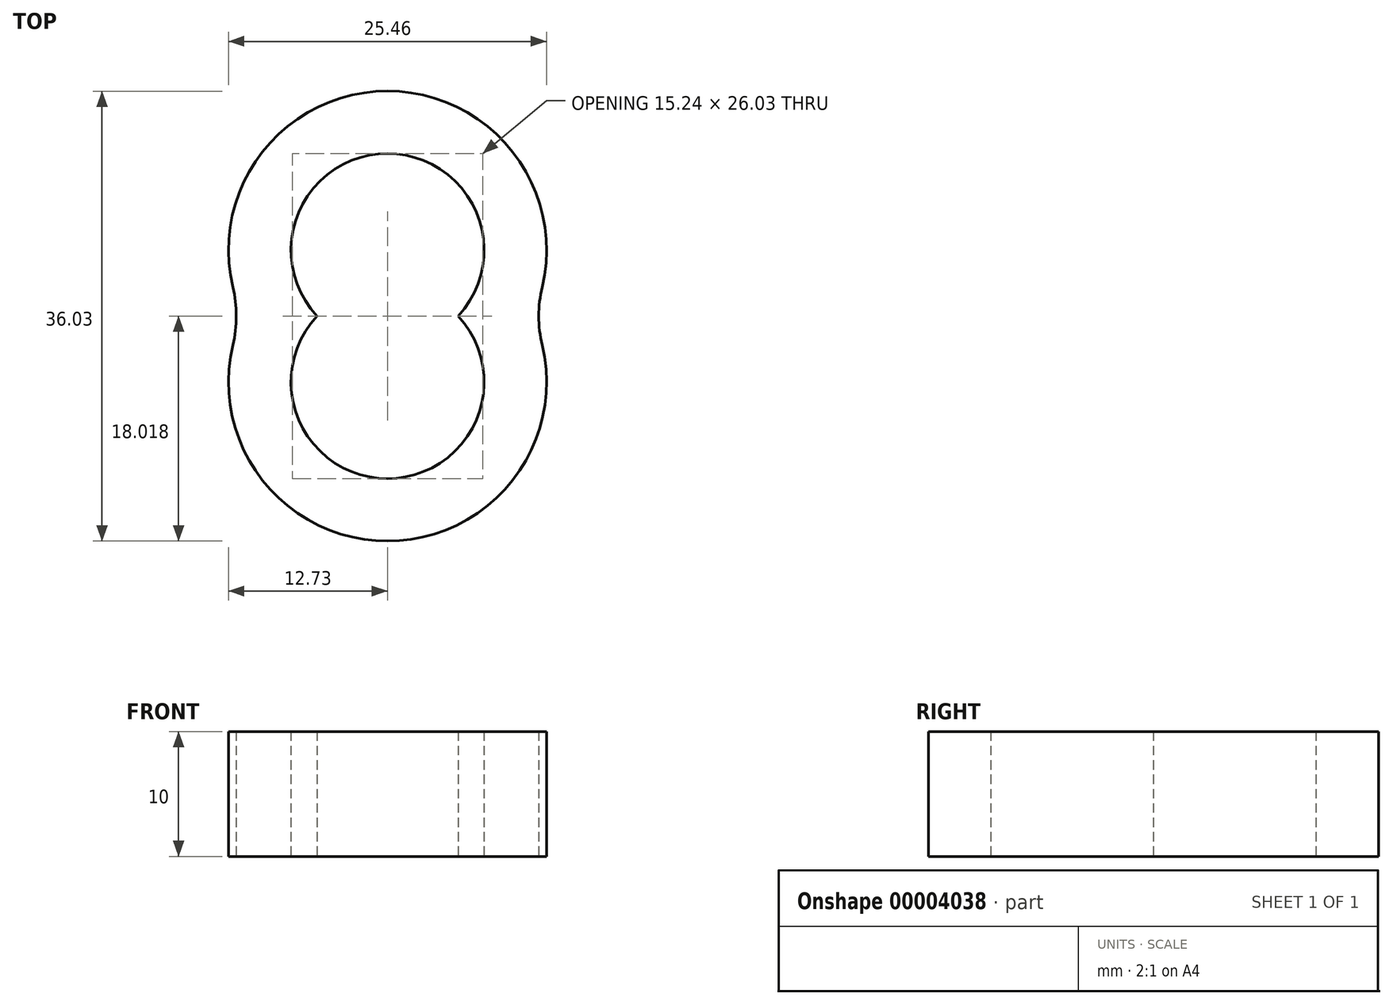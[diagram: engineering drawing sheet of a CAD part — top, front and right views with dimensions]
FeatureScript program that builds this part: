
annotation { "Feature Type Name" : "Feature", "Feature Type Description" : "" }
export const myFeature = defineFeature(function(context is Context, id is Id, definition is map)
    precondition{}
    {
        {
            var Q0;
            Q0=qCreatedBy(makeId("Top.planeOp"),FACE);
            var sketch = newSketch(context, id + "F0", { "sketchPlane" : qUnion([Q0])});
            skArc(sketch, "E0", {"start": v(-78.68, 36.93) * mm, "mid": v(-73.03, 23.91) * mm, "end": v(-67.38, 36.93) * mm});
            skLineSegment(sketch, "E1", {"start": v(-78.68, 36.93) * mm, "end": v(41.42, 36.93) * mm, "construction": true});
            skArc(sketch, "E2.0", {"start": v(-85.41, 34.6) * mm, "mid": v(-73.03, 18.91) * mm, "end": v(-60.65, 34.6) * mm});
            skLineSegment(sketch, "E3", {"start": v(-84.61, 36.93) * mm, "end": v(-78.68, 36.93) * mm});
            skLineSegment(sketch, "E4", {"start": v(-67.38, 36.93) * mm, "end": v(-61.45, 36.93) * mm});
            skArc(sketch, "E5.0.MirrorCS", {"start": v(-78.68, 36.93) * mm, "mid": v(-73.03, 49.94) * mm, "end": v(-67.38, 36.93) * mm});
            skArc(sketch, "E6.0.MirrorCS", {"start": v(-85.41, 39.25) * mm, "mid": v(-73.03, 54.94) * mm, "end": v(-60.65, 39.25) * mm});
            skPoint(sketch, "E7.visualSharp", {"position": v(-61.45, 36.93) * mm});
            skArc(sketch, "E7.filletArc", {"start": v(-60.65, 39.25) * mm, "mid": v(-60.92, 36.93) * mm, "end": v(-60.65, 34.6) * mm});
            skPoint(sketch, "E8.visualSharp", {"position": v(-84.61, 36.93) * mm});
            skArc(sketch, "E8.filletArc", {"start": v(-85.41, 34.6) * mm, "mid": v(-85.14, 36.93) * mm, "end": v(-85.41, 39.25) * mm});
            skArc(sketch, "E9.1.0", {"start": v(-99.44, 9.54) * mm, "mid": v(-103.48, 23.13) * mm, "end": v(-90.79, 16.8) * mm});
            skArc(sketch, "E9.1.1", {"start": v(-106.1, 6.98) * mm, "mid": v(-106.7, 26.96) * mm, "end": v(-87.12, 22.9) * mm});
            skArc(sketch, "E9.1.2", {"start": v(-99.44, 9.54) * mm, "mid": v(-86.75, 3.2) * mm, "end": v(-90.79, 16.8) * mm});
            skArc(sketch, "E9.1.3", {"start": v(-103.1, 3.42) * mm, "mid": v(-83.53, -0.64) * mm, "end": v(-84.13, 19.34) * mm});
            skArc(sketch, "E9.1.4", {"start": v(-87.12, 22.9) * mm, "mid": v(-85.84, 20.95) * mm, "end": v(-84.13, 19.34) * mm});
            skArc(sketch, "E9.1.5", {"start": v(-103.1, 3.42) * mm, "mid": v(-104.39, 5.38) * mm, "end": v(-106.1, 6.98) * mm});
            skArc(sketch, "E9.2.0", {"start": v(-97.73, -24.8) * mm, "mid": v(-109.57, -16.97) * mm, "end": v(-95.77, -13.67) * mm});
            skArc(sketch, "E9.2.1", {"start": v(-101.2, -31.03) * mm, "mid": v(-114.5, -16.1) * mm, "end": v(-96.9, -6.64) * mm});
            skArc(sketch, "E9.2.2", {"start": v(-97.73, -24.8) * mm, "mid": v(-83.94, -21.5) * mm, "end": v(-95.77, -13.67) * mm});
            skArc(sketch, "E9.2.3", {"start": v(-96.61, -31.83) * mm, "mid": v(-79.01, -22.36) * mm, "end": v(-92.31, -7.44) * mm});
            skArc(sketch, "E9.2.4", {"start": v(-96.9, -6.64) * mm, "mid": v(-94.65, -7.3) * mm, "end": v(-92.31, -7.44) * mm});
            skArc(sketch, "E9.2.5", {"start": v(-96.61, -31.83) * mm, "mid": v(-98.86, -31.16) * mm, "end": v(-101.2, -31.03) * mm});
            skArc(sketch, "E9.3.0", {"start": v(-74.36, -50) * mm, "mid": v(-88.46, -51.62) * mm, "end": v(-80, -40.22) * mm});
            skArc(sketch, "E9.3.1", {"start": v(-73, -57) * mm, "mid": v(-92.79, -54.12) * mm, "end": v(-85.39, -35.55) * mm});
            skArc(sketch, "E9.3.2", {"start": v(-74.36, -50) * mm, "mid": v(-65.91, -38.6) * mm, "end": v(-80, -40.22) * mm});
            skArc(sketch, "E9.3.3", {"start": v(-68.98, -54.67) * mm, "mid": v(-61.58, -36.1) * mm, "end": v(-81.36, -33.22) * mm});
            skArc(sketch, "E9.3.4", {"start": v(-85.39, -35.55) * mm, "mid": v(-83.24, -34.62) * mm, "end": v(-81.36, -33.22) * mm});
            skArc(sketch, "E9.3.5", {"start": v(-68.98, -54.67) * mm, "mid": v(-71.13, -55.6) * mm, "end": v(-73, -57) * mm});
            skArc(sketch, "E9.4.0", {"start": v(-40.26, -54.28) * mm, "mid": v(-50.01, -64.58) * mm, "end": v(-50.87, -50.42) * mm});
            skArc(sketch, "E9.4.1", {"start": v(-34.72, -58.77) * mm, "mid": v(-51.72, -69.28) * mm, "end": v(-58, -50.3) * mm});
            skArc(sketch, "E9.4.2", {"start": v(-40.26, -54.28) * mm, "mid": v(-41.11, -40.12) * mm, "end": v(-50.87, -50.42) * mm});
            skArc(sketch, "E9.4.3", {"start": v(-33.13, -54.4) * mm, "mid": v(-39.4, -35.42) * mm, "end": v(-56.4, -45.93) * mm});
            skArc(sketch, "E9.4.4", {"start": v(-58, -50.3) * mm, "mid": v(-56.94, -48.2) * mm, "end": v(-56.4, -45.93) * mm});
            skArc(sketch, "E9.4.5", {"start": v(-33.13, -54.4) * mm, "mid": v(-34.18, -56.5) * mm, "end": v(-34.72, -58.77) * mm});
            skArc(sketch, "E9.5.0", {"start": v(-11.38, -35.64) * mm, "mid": v(-12.23, -49.8) * mm, "end": v(-21.99, -39.5) * mm});
            skArc(sketch, "E9.5.1", {"start": v(-4.25, -35.52) * mm, "mid": v(-10.52, -54.5) * mm, "end": v(-27.53, -44) * mm});
            skArc(sketch, "E9.5.2", {"start": v(-11.38, -35.64) * mm, "mid": v(-21.14, -25.34) * mm, "end": v(-21.99, -39.5) * mm});
            skArc(sketch, "E9.5.3", {"start": v(-5.84, -31.15) * mm, "mid": v(-22.85, -20.64) * mm, "end": v(-29.12, -39.62) * mm});
            skArc(sketch, "E9.5.4", {"start": v(-27.53, -44) * mm, "mid": v(-28.06, -41.71) * mm, "end": v(-29.12, -39.62) * mm});
            skArc(sketch, "E9.5.5", {"start": v(-5.84, -31.15) * mm, "mid": v(-5.3, -33.43) * mm, "end": v(-4.25, -35.52) * mm});
            skArc(sketch, "E9.6.0", {"start": v(-1.24, -2.8) * mm, "mid": v(7.2, -14.2) * mm, "end": v(-6.88, -12.58) * mm});
            skArc(sketch, "E9.6.1", {"start": v(4.14, 1.87) * mm, "mid": v(11.54, -16.7) * mm, "end": v(-8.24, -19.57) * mm});
            skArc(sketch, "E9.6.2", {"start": v(-1.24, -2.8) * mm, "mid": v(-15.33, -1.18) * mm, "end": v(-6.88, -12.58) * mm});
            skArc(sketch, "E9.6.3", {"start": v(0.12, 4.2) * mm, "mid": v(-19.66, 1.32) * mm, "end": v(-12.27, -17.25) * mm});
            skArc(sketch, "E9.6.4", {"start": v(-8.24, -19.57) * mm, "mid": v(-10.12, -18.17) * mm, "end": v(-12.27, -17.25) * mm});
            skArc(sketch, "E9.6.5", {"start": v(0.12, 4.2) * mm, "mid": v(2, 2.8) * mm, "end": v(4.14, 1.87) * mm});
            skArc(sketch, "E9.7.0", {"start": v(-14.58, 28.88) * mm, "mid": v(-0.78, 25.58) * mm, "end": v(-12.62, 17.76) * mm});
            skArc(sketch, "E9.7.1", {"start": v(-13.46, 35.92) * mm, "mid": v(4.14, 26.45) * mm, "end": v(-9.16, 11.53) * mm});
            skArc(sketch, "E9.7.2", {"start": v(-14.58, 28.88) * mm, "mid": v(-26.42, 21.06) * mm, "end": v(-12.62, 17.76) * mm});
            skArc(sketch, "E9.7.3", {"start": v(-18.04, 35.1) * mm, "mid": v(-31.34, 20.19) * mm, "end": v(-13.74, 10.72) * mm});
            skArc(sketch, "E9.7.4", {"start": v(-9.16, 11.53) * mm, "mid": v(-11.5, 11.4) * mm, "end": v(-13.74, 10.72) * mm});
            skArc(sketch, "E9.7.5", {"start": v(-18.04, 35.1) * mm, "mid": v(-15.7, 35.24) * mm, "end": v(-13.46, 35.92) * mm});
            skArc(sketch, "E9.8.0", {"start": v(-45.16, 44.57) * mm, "mid": v(-32.47, 50.9) * mm, "end": v(-36.51, 37.3) * mm});
            skArc(sketch, "E9.8.1", {"start": v(-48.83, 50.68) * mm, "mid": v(-29.26, 54.74) * mm, "end": v(-29.86, 34.76) * mm});
            skArc(sketch, "E9.8.2", {"start": v(-45.16, 44.57) * mm, "mid": v(-49.2, 30.97) * mm, "end": v(-36.51, 37.3) * mm});
            skArc(sketch, "E9.8.3", {"start": v(-51.82, 47.12) * mm, "mid": v(-52.42, 27.14) * mm, "end": v(-32.85, 31.2) * mm});
            skArc(sketch, "E9.8.4", {"start": v(-29.86, 34.76) * mm, "mid": v(-31.56, 33.15) * mm, "end": v(-32.85, 31.2) * mm});
            skArc(sketch, "E9.8.5", {"start": v(-51.82, 47.12) * mm, "mid": v(-50.12, 48.72) * mm, "end": v(-48.83, 50.68) * mm});
            skPoint(sketch, "E9.center", {"position": v(-51.43, -5.29) * mm});
            skSolve(sketch);
        }
        {
            var Q0;
            Q0=makeQuery(id+"F0.imprint","IMPRINT",FACE,{"disambiguationData":[TD([[makeQuery(id+"F0.imprint","IMPRINT",EDGE,{"derivedFrom":sQuery(id+"F0.wireOp",EDGE,"E3")}),1.0]])]});
            var Q1;
            Q1=makeQuery(id+"F0.imprint","IMPRINT",FACE,{"disambiguationData":[TD([[makeQuery(id+"F0.imprint","IMPRINT",EDGE,{"derivedFrom":sQuery(id+"F0.wireOp",EDGE,"E0")}),-1.0]])]});
            extrude(context, id + "F1", {"entities" : qUnion([Q0, Q1]), "depth" : 10 * mm});
        }
    });
